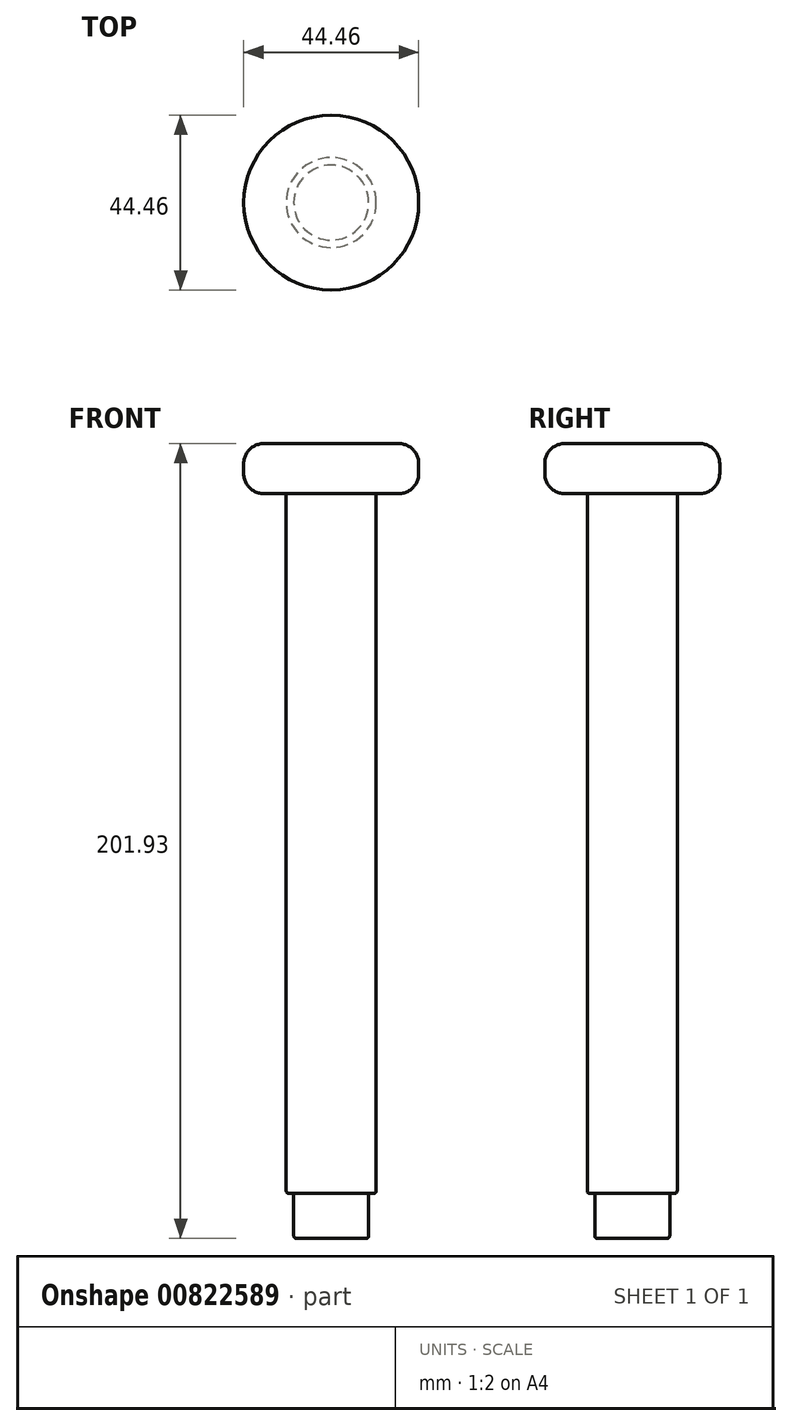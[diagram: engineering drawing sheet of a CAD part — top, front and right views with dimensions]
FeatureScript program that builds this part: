
annotation { "Feature Type Name" : "Feature", "Feature Type Description" : "" }
export const myFeature = defineFeature(function(context is Context, id is Id, definition is map)
    precondition{}
    {
        {
            var Q0;
            Q0=qCreatedBy(makeId("Top.planeOp"),FACE);
            var sketch = newSketch(context, id + "F0", { "sketchPlane" : qUnion([Q0])});
            skCircle(sketch, "E0", {"center": v(0, 0) * mm, "radius": 9.53 * mm});
            skSolve(sketch);
        }
        {
            var Q0;
            Q0 = qSketchRegion(id + "F0", true);
            extrude(context, id + "F1", {"entities" : qUnion([Q0]), "depth" : 11.43 * mm, "offsetDistance" : 25.4 * mm});
        }
        {
            var Q0;
            Q0=makeQuery(id+"F1.opExtrude","CAP_FACE",FACE,{"disambiguationData":[OSD([sQuery(id+"F0.wireOp",EDGE,"E0")])],"isStart":false});
            var sketch = newSketch(context, id + "F2", { "sketchPlane" : qUnion([Q0])});
            skCircle(sketch, "E1", {"center": v(0, 0) * mm, "radius": 11.43 * mm});
            skSolve(sketch);
        }
        {
            var Q0;
            Q0 = qSketchRegion(id + "F2", true);
            extrude(context, id + "F3", {"entities" : qUnion([Q0]), "operationType" : NewBodyOperationType.ADD, "depth" : 177.8 * mm, "offsetDistance" : 25.4 * mm});
        }
        {
            var Q0;
            Q0=makeQuery(id+"F3.opExtrude","CAP_FACE",FACE,{"disambiguationData":[OSD([sQuery(id+"F2.wireOp",EDGE,"E1")])],"isStart":false});
            var sketch = newSketch(context, id + "F4", { "sketchPlane" : qUnion([Q0])});
            skCircle(sketch, "E2", {"center": v(0, 0) * mm, "radius": 22.23 * mm});
            skSolve(sketch);
        }
        {
            var Q0;
            Q0 = qSketchRegion(id + "F4", true);
            extrude(context, id + "F5", {"entities" : qUnion([Q0]), "operationType" : NewBodyOperationType.ADD, "depth" : 12.7 * mm, "offsetDistance" : 25.4 * mm});
        }
        {
            var Q0;
            Q0=makeQuery(id+"F5.opExtrude","CAP_FACE",FACE,{"disambiguationData":[OSD([sQuery(id+"F4.wireOp",EDGE,"E2")])],"isStart":false});
            var Q1;
            Q1=makeQuery(id+"F5.opExtrude","CAP_EDGE",EDGE,{"disambiguationData":[OSD([sQuery(id+"F4.wireOp",EDGE,"E2")])],"isStart":true});
            fillet(context, id + "F6", {"entities" : qUnion([Q0, Q1]), "tangentPropagation" : true, "radius" : 5.08 * mm, "defaultsChanged" : false, "vertexSettings" : [], "allowEdgeOverflow" : false});
        }
        {
            var Q0;
            Q0=makeQuery(id+"F3.opExtrude","CAP_EDGE",EDGE,{"disambiguationData":[OSD([sQuery(id+"F2.wireOp",EDGE,"E1")])],"isStart":true});
            var Q1;
            Q1=makeQuery(id+"F1.opExtrude","CAP_EDGE",EDGE,{"disambiguationData":[OSD([sQuery(id+"F0.wireOp",EDGE,"E0")])],"isStart":true});
            fillet(context, id + "F7", {"entities" : qUnion([Q0, Q1]), "tangentPropagation" : true, "radius" : 0.64 * mm, "defaultsChanged" : true, "vertexSettings" : [], "allowEdgeOverflow" : false});
        }
    });
